# Revit family: LED WALL TUBE 03_LK0327WW.24
name_source: partatom
category: Luminarias
units: mm (PartAtom-declared; Revit-internal decimal feet)

## family parameters
Compartido = No
Corte con vacíos al cargar = No
Cota de conector redondo = Diámetro de uso
Origen de luz = Sí
Punto de cálculo de habitación = No
Se basa en plano de trabajo = Sí
Siempre vertical = No
Tipo de pieza = Normal

## types (1)
- LED WALL TUBE 03_LK0327WW.24
    Archivo de red fotométrica = LK0327WW.IES
    Cambio de temperatura de color de luz atenuada = <Ninguno>
    Comentarios de vataje = 100-277V
    Descripción = LUMINARIA DIRIGIBLE (28 GRADOS POSITIVOS Y NEGATIVOS) TIPO ARBOTANTE, DE MATERIAL DE ALUMINIO FUNDIDO A PRESION, CUBIERTO CON POLVO GRIS OSCURO Y VIDRIO TEMPLADO DE 4MM CON UN PESO DE 1KG, CON 4 LED TIPO NICHIA CON UNA POTENCIA TOTAL DE 12.6W, 956 LUMENES, TEMPERATURA EN BLANCO CALIDO 3000K, IRC 80, IP 66, APERTURA DE  24 GRADOS EN STOCK, CORRIENTE DE OPERACIÓN 107mA, CABLE DE 2M, ALIMENTADO A 100-277VAC
    Elevación por defecto = 0 mm  [stored 0 ft]
    Fabricante = BRILLANT
    Filtro de color = 16777215
    Lámpara = NICHIA
    Modelo = LK0327WW.24
    Watt per fixture = 12.6
    Ángulo de inclinación = 60.00°

note: [stored X ft] marks values corroborated as IEEE doubles in the binary element streams (Revit-internal decimal feet)

## geometry (parser evidence)
native form markers: Blend x2
no freeform markers — native parametric forms only
